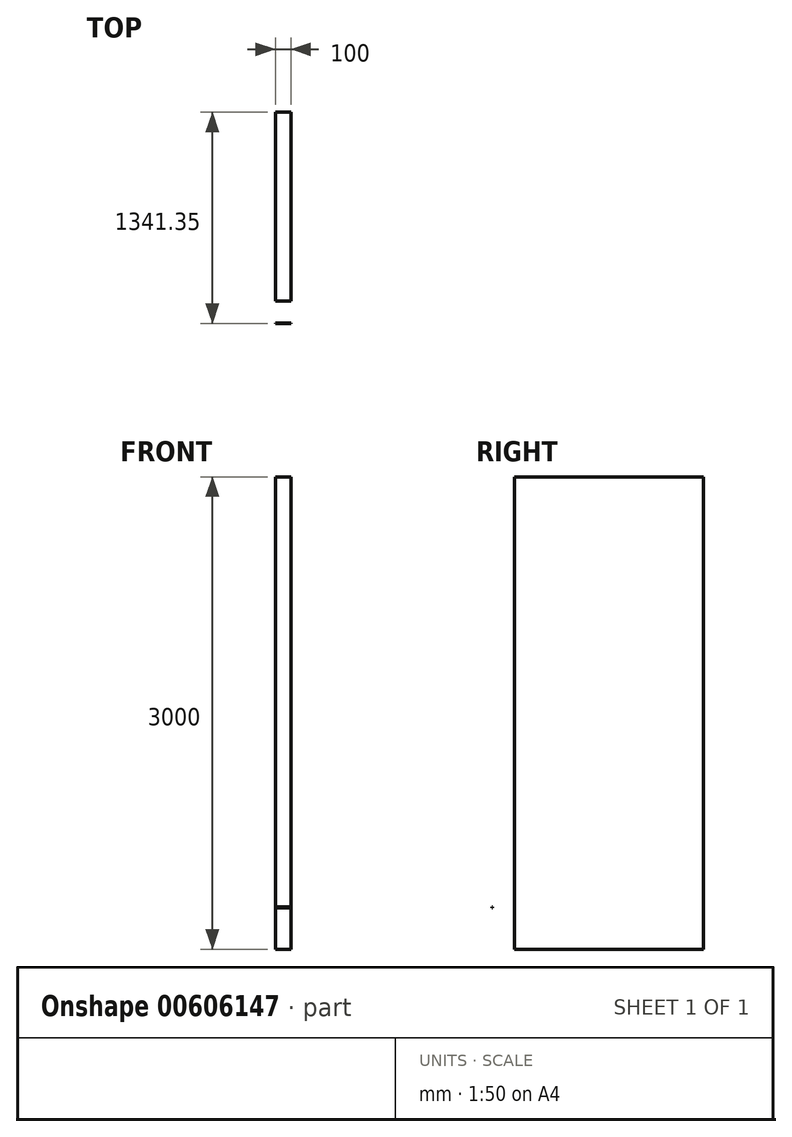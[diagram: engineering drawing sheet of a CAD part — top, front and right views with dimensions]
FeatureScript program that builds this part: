
annotation { "Feature Type Name" : "Feature", "Feature Type Description" : "" }
export const myFeature = defineFeature(function(context is Context, id is Id, definition is map)
    precondition{}
    {
        {
            var Q0;
            Q0=qCreatedBy(makeId("Right.planeOp"),FACE);
            var sketch = newSketch(context, id + "F0", { "sketchPlane" : qUnion([Q0])});
            skLineSegment(sketch, "E0.bottom", {"start": v(-206, 417.64) * mm, "end": v(-203.78, 417.64) * mm});
            skLineSegment(sketch, "E0.top", {"start": v(-206, 423.72) * mm, "end": v(-203.78, 423.72) * mm});
            skLineSegment(sketch, "E0.left", {"start": v(-206, 417.64) * mm, "end": v(-206, 423.72) * mm});
            skLineSegment(sketch, "E0.right", {"start": v(-203.78, 417.64) * mm, "end": v(-203.78, 423.72) * mm});
            skLineSegment(sketch, "E1.bottom", {"start": v(-64.64, 3154.2) * mm, "end": v(1135.36, 3154.2) * mm});
            skLineSegment(sketch, "E1.top", {"start": v(-64.64, 154.2) * mm, "end": v(1135.36, 154.2) * mm});
            skLineSegment(sketch, "E1.left", {"start": v(-64.64, 3154.2) * mm, "end": v(-64.64, 154.2) * mm});
            skLineSegment(sketch, "E1.right", {"start": v(1135.36, 3154.2) * mm, "end": v(1135.36, 154.2) * mm});
            skSolve(sketch);
        }
        {
            var Q0;
            Q0=qSketchRegion(id+"F0",true);
            extrude(context, id + "F1", {"entities" : qUnion([Q0]), "depth" : 100 * mm, "offsetDistance" : 25 * mm});
        }
    });
